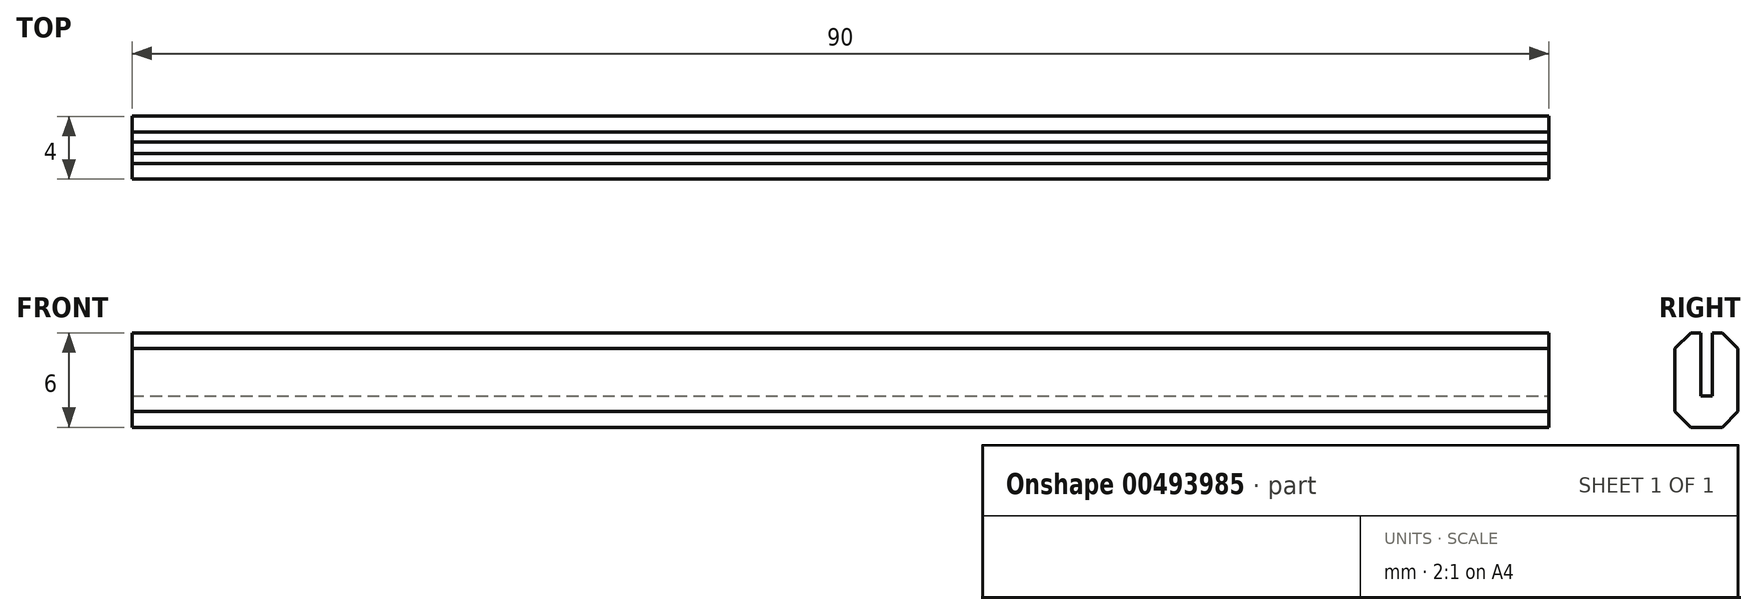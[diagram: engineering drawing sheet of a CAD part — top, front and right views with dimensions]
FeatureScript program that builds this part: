
annotation { "Feature Type Name" : "Feature", "Feature Type Description" : "" }
export const myFeature = defineFeature(function(context is Context, id is Id, definition is map)
    precondition{}
    {
        {
            var Q0;
            Q0=qCreatedBy(makeId("Top.planeOp"),FACE);
            var sketch = newSketch(context, id + "F0", { "sketchPlane" : qUnion([Q0])});
            skLineSegment(sketch, "E0.bottom", {"start": v(-37.47, 1.7) * mm, "end": v(52.53, 1.7) * mm});
            skLineSegment(sketch, "E0.top", {"start": v(-37.47, -2.3) * mm, "end": v(52.53, -2.3) * mm});
            skLineSegment(sketch, "E0.left", {"start": v(-37.47, 1.7) * mm, "end": v(-37.47, -2.3) * mm});
            skLineSegment(sketch, "E0.right", {"start": v(52.53, 1.7) * mm, "end": v(52.53, -2.3) * mm});
            skLineSegment(sketch, "E1", {"start": v(-37.47, 0.07) * mm, "end": v(-37.47, -0.68) * mm, "construction": true});
            skPoint(sketch, "E2", {"position": v(-37.47, -0.3) * mm});
            skLineSegment(sketch, "E3", {"start": v(-37.47, 0.07) * mm, "end": v(52.53, 0.07) * mm});
            skLineSegment(sketch, "E4", {"start": v(-37.47, -0.68) * mm, "end": v(52.53, -0.68) * mm});
            skSolve(sketch);
        }
        {
            var Q0;
            {var subQ0=sQuery(id+"F0.wireOp",EDGE,"E0.top");Q0=makeQuery(id+"F0.imprint","IMPRINT",FACE,{"disambiguationData":[TD([[makeQuery(id+"F0.imprint","IMPRINT",EDGE,{"derivedFrom":subQ0}),1.0]])]});}
            var Q1;
            {var subQ0=sQuery(id+"F0.wireOp",EDGE,"E3");Q1=makeQuery(id+"F0.imprint","IMPRINT",FACE,{"disambiguationData":[TD([[makeQuery(id+"F0.imprint","IMPRINT",EDGE,{"derivedFrom":subQ0}),-1.0]])]});}
            var Q2;
            {var subQ0=sQuery(id+"F0.wireOp",EDGE,"E0.bottom");Q2=makeQuery(id+"F0.imprint","IMPRINT",FACE,{"disambiguationData":[TD([[makeQuery(id+"F0.imprint","IMPRINT",EDGE,{"derivedFrom":subQ0}),-1.0]])]});}
            extrude(context, id + "F1", {"entities" : qUnion([Q0, Q1, Q2]), "oppositeDirection" : true, "depth" : 2 * mm});
        }
        {
            var Q0;
            {var subQ0=sQuery(id+"F0.wireOp",EDGE,"E0.bottom");Q0=makeQuery(id+"F0.imprint","IMPRINT",FACE,{"disambiguationData":[TD([[makeQuery(id+"F0.imprint","IMPRINT",EDGE,{"derivedFrom":subQ0}),-1.0]])]});}
            var Q1;
            {var subQ0=sQuery(id+"F0.wireOp",EDGE,"E0.top");Q1=makeQuery(id+"F0.imprint","IMPRINT",FACE,{"disambiguationData":[TD([[makeQuery(id+"F0.imprint","IMPRINT",EDGE,{"derivedFrom":subQ0}),1.0]])]});}
            extrude(context, id + "F2", {"entities" : qUnion([Q0, Q1]), "operationType" : NewBodyOperationType.ADD, "depth" : 4 * mm});
        }
        {
            var Q0;
            Q0=makeQuery(id+"F1.opExtrude","CAP_EDGE",EDGE,{"disambiguationData":[OSD([sQuery(id+"F0.wireOp",EDGE,"E0.bottom")])],"isStart":false});
            var Q1;
            Q1=makeQuery(id+"F1.opExtrude","CAP_EDGE",EDGE,{"disambiguationData":[OSD([sQuery(id+"F0.wireOp",EDGE,"E0.top")])],"isStart":false});
            var Q2;
            Q2=makeQuery(id+"F2.opExtrude","CAP_EDGE",EDGE,{"disambiguationData":[OSD([sQuery(id+"F0.wireOp",EDGE,"E0.bottom")])],"isStart":false});
            var Q3;
            Q3=makeQuery(id+"F2.opExtrude","CAP_EDGE",EDGE,{"disambiguationData":[OSD([sQuery(id+"F0.wireOp",EDGE,"E0.top")])],"isStart":false});
            chamfer(context, id + "F3", {"entities" : qUnion([Q0, Q1, Q2, Q3]), "chamferType" : ChamferType.OFFSET_ANGLE, "width" : 1 * mm, "oppositeDirection" : false, "angle" : 45 * degree, "tangentPropagation" : true});
        }
    });
